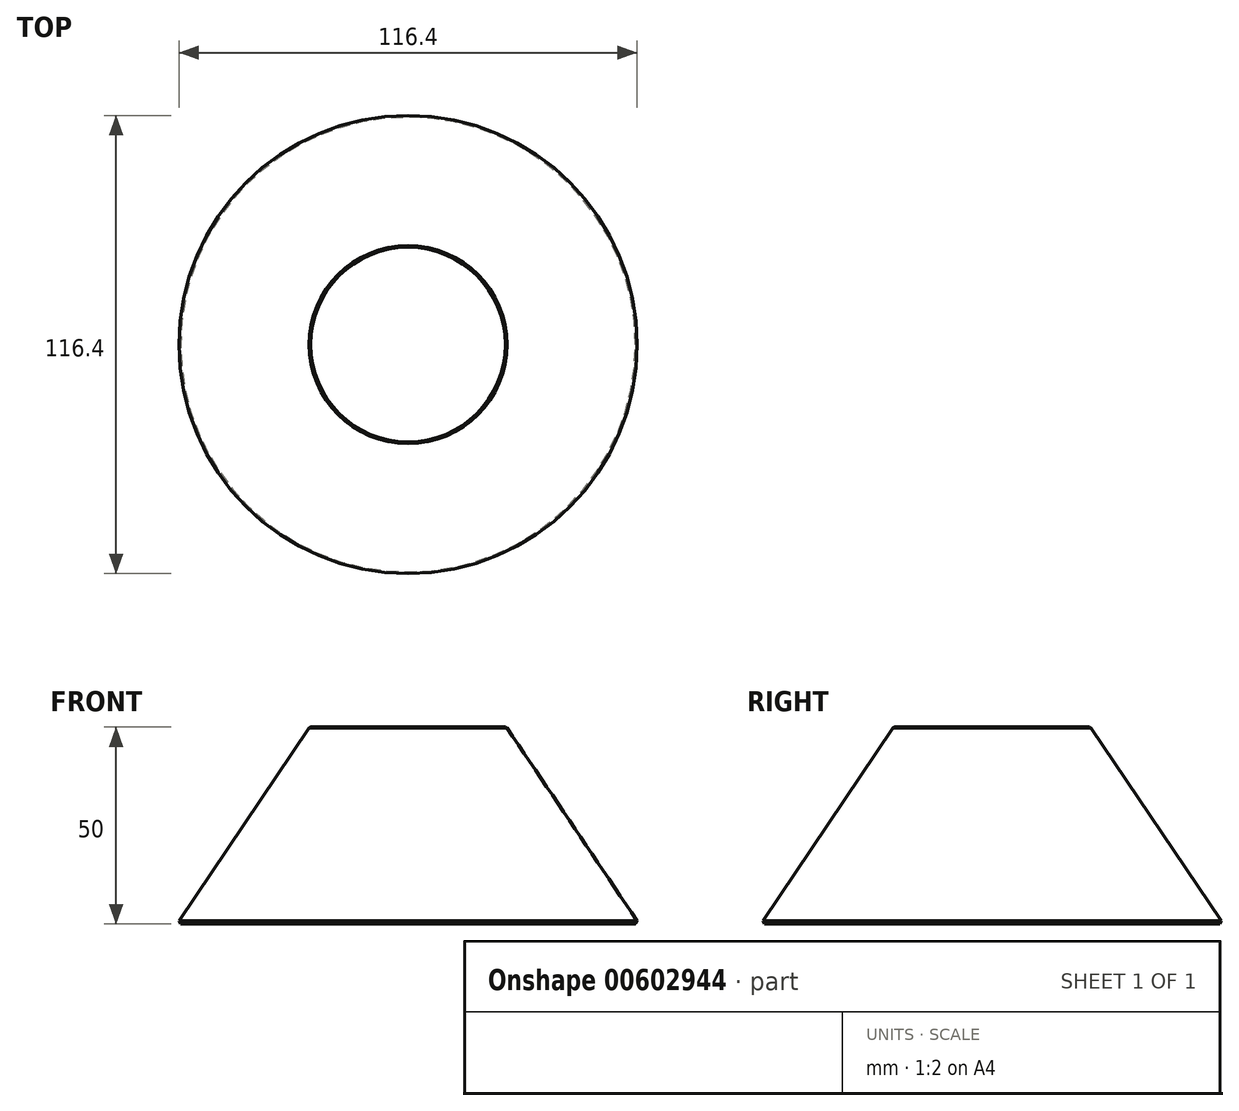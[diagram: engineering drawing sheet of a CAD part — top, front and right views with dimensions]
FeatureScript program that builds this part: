
annotation { "Feature Type Name" : "Feature", "Feature Type Description" : "" }
export const myFeature = defineFeature(function(context is Context, id is Id, definition is map)
    precondition{}
    {
        {
            var Q0;
            Q0=qCreatedBy(makeId("Front.planeOp"),FACE);
            var sketch = newSketch(context, id + "F0", { "sketchPlane" : qUnion([Q0])});
            skLineSegment(sketch, "E0", {"start": v(0, 0) * mm, "end": v(0, 50) * mm});
            skLineSegment(sketch, "E1", {"start": v(25, 50) * mm, "end": v(58.73, 0) * mm});
            skLineSegment(sketch, "E2", {"start": v(58.73, 0) * mm, "end": v(0, 0) * mm});
            skLineSegment(sketch, "E3", {"start": v(0, 50) * mm, "end": v(25, 50) * mm});
            skSolve(sketch);
        }
        {
            var Q0;
            Q0=makeQuery(id+"F0.imprint","IMPRINT",FACE,{"disambiguationData":[TD([[makeQuery(id+"F0.imprint","IMPRINT",EDGE,{"derivedFrom":sQuery(id+"F0.wireOp",EDGE,"E0")}),-1.0]])]});
            var Q1;
            Q1=sQuery(id+"F0.wireOp",EDGE,"E0");
            revolve(context, id + "F1", {"entities" : qUnion([Q0]), "axis" : qUnion([Q1]), "revolveType" : RevolveType.FULL});
        }
        {
            var Q0;
            Q0=makeQuery(id+"F1.opRevolve","SWEPT_FACE",FACE,{"disambiguationData":[OSD([sQuery(id+"F0.wireOp",EDGE,"E1")])]});
            chamfer(context, id + "F2", {"entities" : qUnion([Q0]), "width" : 0.5 * mm, "tangentPropagation" : true});
        }
    });
